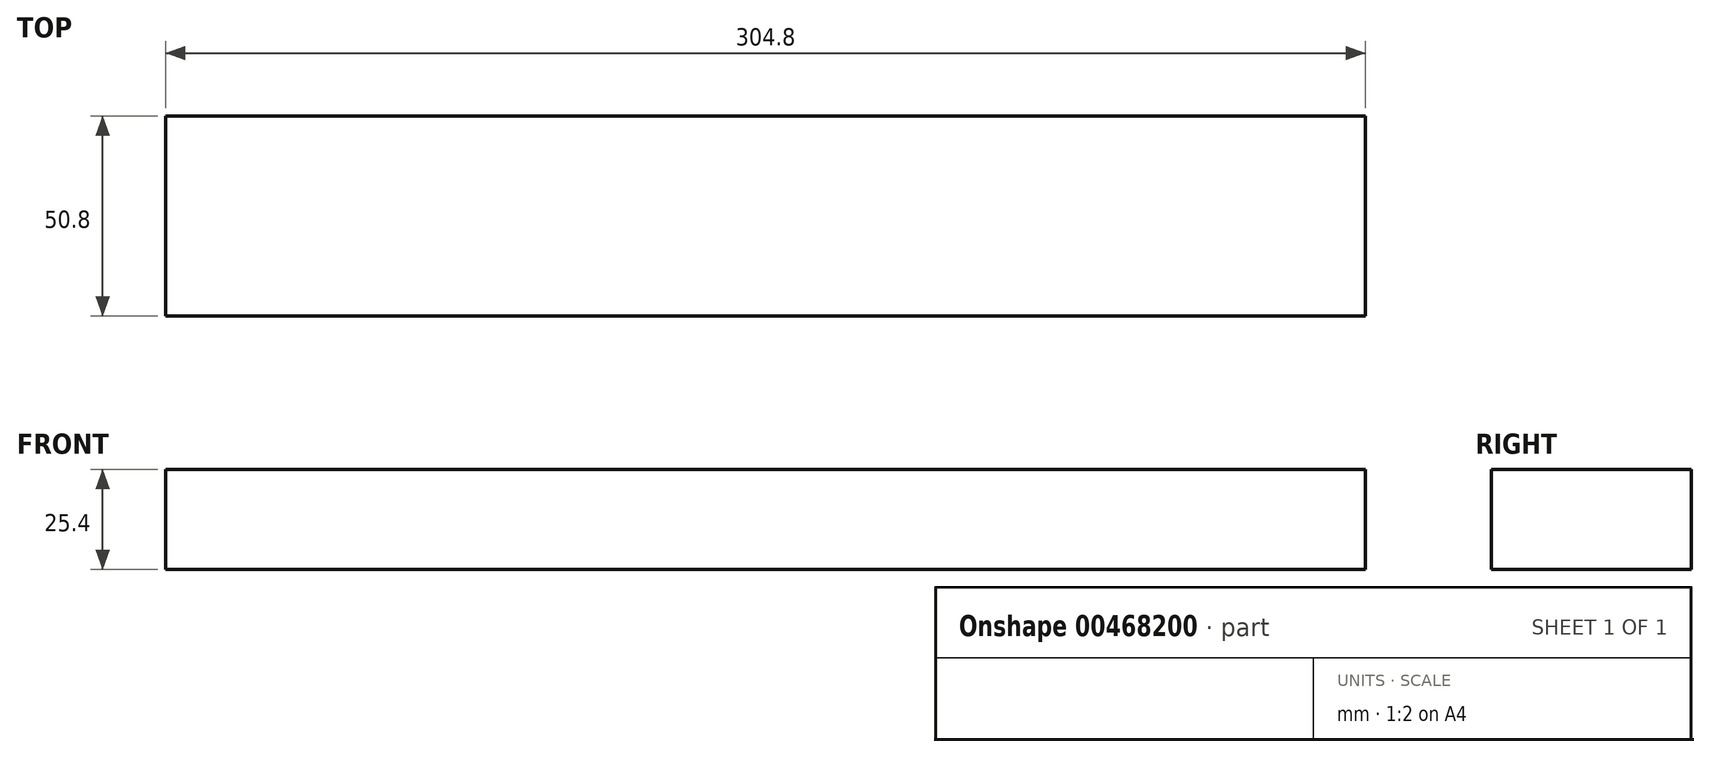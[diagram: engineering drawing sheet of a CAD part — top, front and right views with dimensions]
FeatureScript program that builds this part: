
annotation { "Feature Type Name" : "Feature", "Feature Type Description" : "" }
export const myFeature = defineFeature(function(context is Context, id is Id, definition is map)
    precondition{}
    {
        {
            var Q0;
            Q0=qCreatedBy(makeId("Top.planeOp"),FACE);
            var sketch = newSketch(context, id + "F0", { "sketchPlane" : qUnion([Q0])});
            skLineSegment(sketch, "E0.bottom", {"start": v(0, 0) * mm, "end": v(304.8, 0) * mm});
            skLineSegment(sketch, "E0.top", {"start": v(0, 50.8) * mm, "end": v(304.8, 50.8) * mm});
            skLineSegment(sketch, "E0.left", {"start": v(0, 0) * mm, "end": v(0, 50.8) * mm});
            skLineSegment(sketch, "E0.right", {"start": v(304.8, 0) * mm, "end": v(304.8, 50.8) * mm});
            skSolve(sketch);
        }
        {
            var Q0;
            Q0=makeQuery(id+"F0.imprint","IMPRINT",FACE,{"disambiguationData":[TD([[makeQuery(id+"F0.imprint","IMPRINT",EDGE,{"derivedFrom":sQuery(id+"F0.wireOp",EDGE,"E0.bottom")}),1.0]])]});
            extrude(context, id + "F1", {"entities" : qUnion([Q0]), "depth" : 25.4 * mm});
        }
    });
